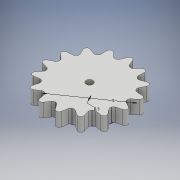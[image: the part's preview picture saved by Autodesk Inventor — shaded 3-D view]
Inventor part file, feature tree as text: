
AUTODESK INVENTOR PART (.ipt)
format: ipt  version: 2018 (Build 220112000, 112)  size: 201,728 bytes
history: native  units: mm
features: extrude x3, sketch x2, other x1, fillet x1, pattern_circular x1
ambient origin geometry x8: Origin, YZ Plane, XZ Plane, XY Plane, X Axis, Y Axis, Z Axis, Center Point
bodies: Body1 (feature_tree)
feature tree (8):
  other  "Sólido1"
  sketch  "Boceto1"  dims[d0=5.0mm d1=1.0mm d2=0.0mm]
  extrude  "Extrusión1"  Depth=1.0mm TaperAngle=0.0deg
  extrude  "Extrusión2"  Depth=1.0mm
  fillet  "Empalme1"  Radius=2.2mm
  pattern_circular  "Patrón circular1"  [2 undecoded]
  extrude  "Extrusión3"  Depth=0.2mm
  sketch  "Boceto2"  dims[d3=0.25mm d4=1.0mm d5=2.2mm d6=1.0mm d7=0.0mm d8=0.2mm d9=150.0mm d10=360.0deg d12=0.5mm d13=1.0mm d14=0.0mm]
note: 2 required parameter values undecoded (feature->parameter linkage not recoverable at this tier; creation-order binding heuristic only, values carry confidence <= 0.55)
